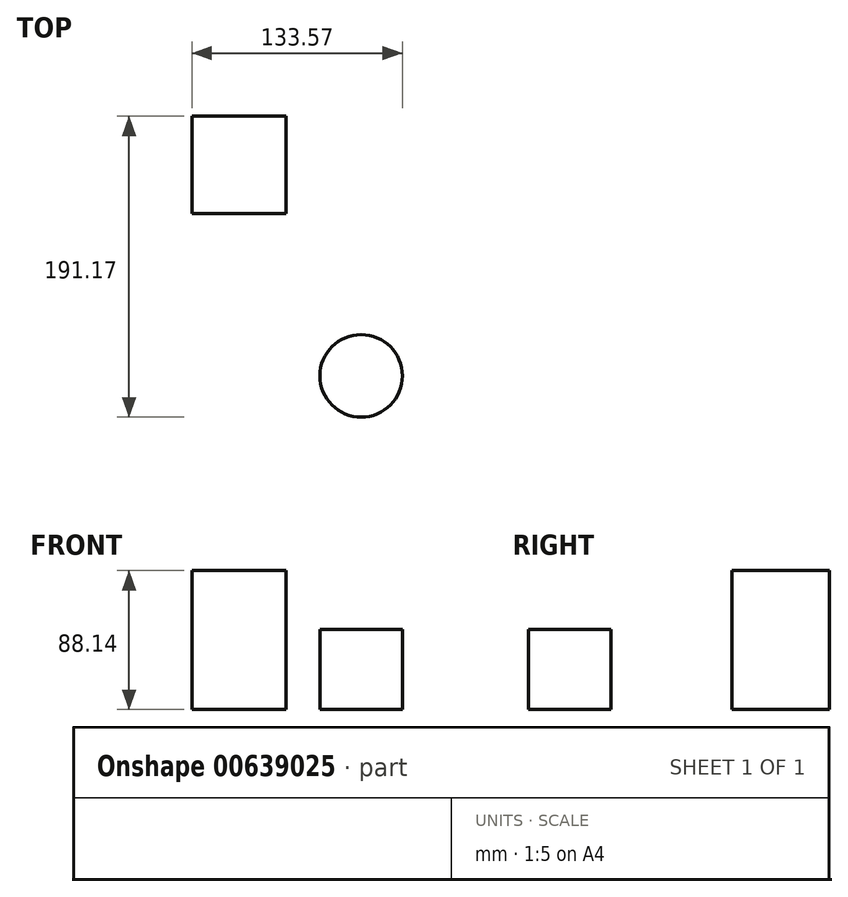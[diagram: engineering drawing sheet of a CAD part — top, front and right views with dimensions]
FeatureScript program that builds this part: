
annotation { "Feature Type Name" : "Feature", "Feature Type Description" : "" }
export const myFeature = defineFeature(function(context is Context, id is Id, definition is map)
    precondition{}
    {
        {
            var Q0;
            Q0=qCreatedBy(makeId("Top.planeOp"),FACE);
            var sketch = newSketch(context, id + "F0", { "sketchPlane" : qUnion([Q0])});
            skLineSegment(sketch, "E0.bottom", {"start": v(0, 0) * mm, "end": v(-59.64, 0) * mm});
            skLineSegment(sketch, "E0.top", {"start": v(0, 61.83) * mm, "end": v(-59.64, 61.83) * mm});
            skLineSegment(sketch, "E0.left", {"start": v(0, 0) * mm, "end": v(0, 61.83) * mm});
            skLineSegment(sketch, "E0.right", {"start": v(-59.64, 0) * mm, "end": v(-59.64, 61.83) * mm});
            skSolve(sketch);
        }
        {
            var Q0;
            Q0=makeQuery(id+"F0.imprint","IMPRINT",FACE,{"disambiguationData":[TD([[makeQuery(id+"F0.imprint","IMPRINT",EDGE,{"derivedFrom":sQuery(id+"F0.wireOp",EDGE,"E0.bottom")}),-1.0]])]});
            extrude(context, id + "F1", {"entities" : qUnion([Q0]), "depth" : 88.14 * mm, "offsetDistance" : 25.4 * mm});
        }
        {
            var Q0;
            Q0=qCreatedBy(makeId("Top.planeOp"),FACE);
            var sketch = newSketch(context, id + "F2", { "sketchPlane" : qUnion([Q0])});
            skCircle(sketch, "E1", {"center": v(47.72, -103.14) * mm, "radius": 26.2 * mm});
            skSolve(sketch);
        }
        {
            var Q0;
            Q0 = qSketchRegion(id + "F2", true);
            extrude(context, id + "F3", {"entities" : qUnion([Q0]), "depth" : 25.4 * mm, "offsetDistance" : 25.4 * mm});
        }
        {
            var Q0;
            Q0=makeQuery(id+"F3.opExtrude","CAP_FACE",FACE,{"disambiguationData":[OSD([sQuery(id+"F2.wireOp",EDGE,"E1")])],"isStart":false});
            extrude(context, id + "F4", {"entities" : qUnion([Q0]), "operationType" : NewBodyOperationType.ADD, "depth" : 25.4 * mm, "offsetDistance" : 25.4 * mm});
        }
    });
